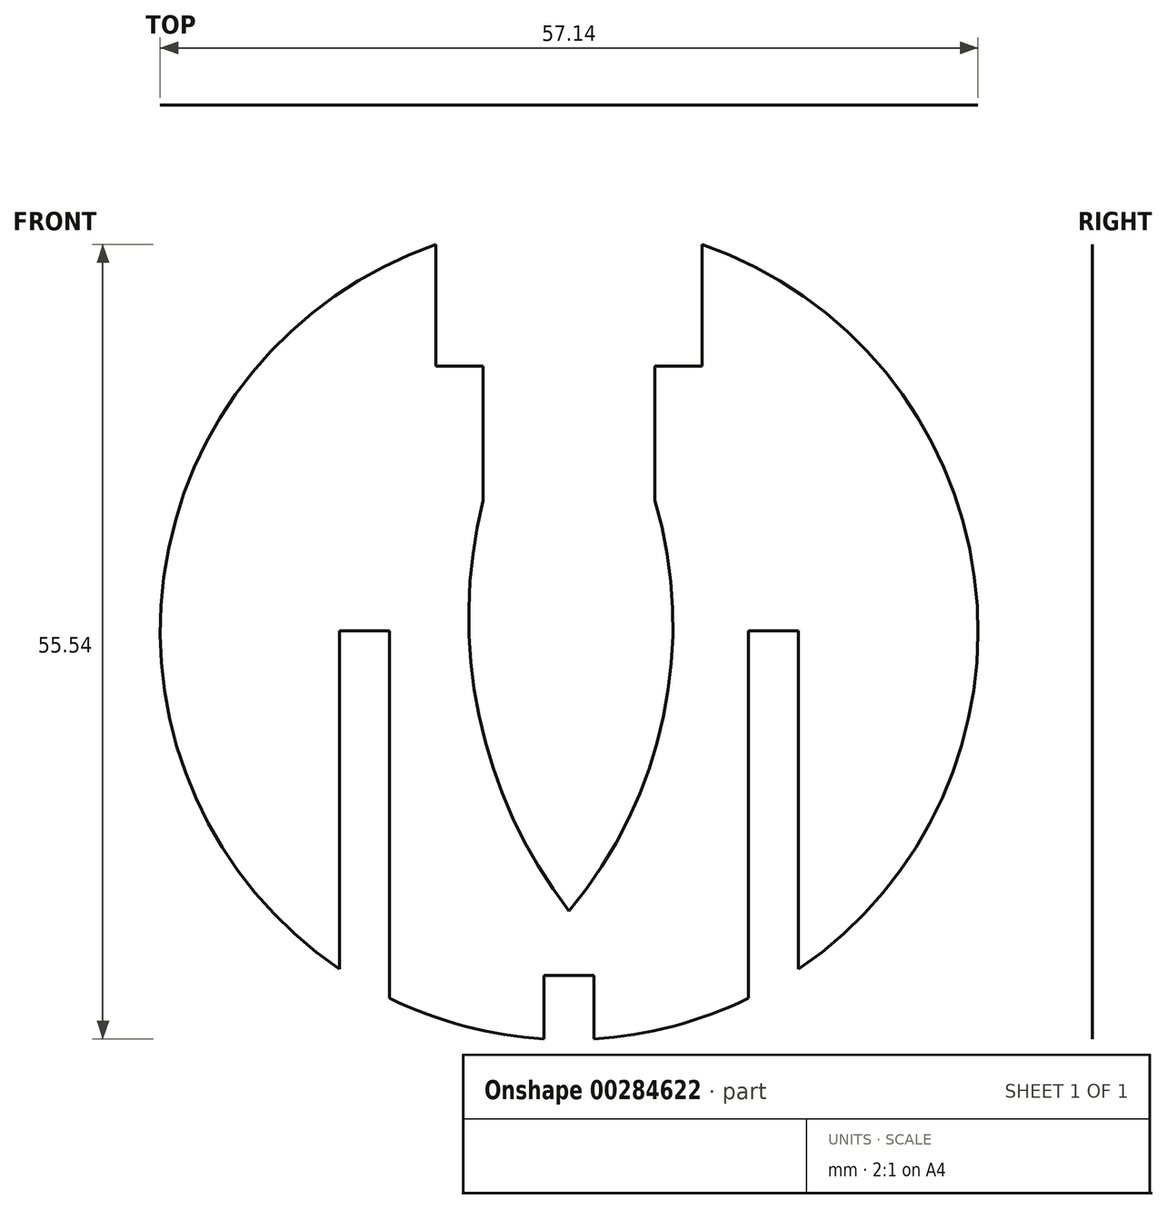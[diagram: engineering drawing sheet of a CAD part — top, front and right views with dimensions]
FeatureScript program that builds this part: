
annotation { "Feature Type Name" : "Feature", "Feature Type Description" : "" }
export const myFeature = defineFeature(function(context is Context, id is Id, definition is map)
    precondition{}
    {
        {
            var Q0;
            Q0=qCreatedBy(makeId("Front.planeOp"),FACE);
            var sketch = newSketch(context, id + "F0", { "sketchPlane" : qUnion([Q0])});
            skCircle(sketch, "E0", {"center": v(0, 0) * mm, "radius": 28.58 * mm});
            skSolve(sketch);
        }
        {
            var Q0;
            Q0 = qSketchRegion(id + "F0", true);
            extrude(context, id + "F1", {"entities" : qUnion([Q0]), "depth" : 1 / 203.2 * mm});
        }
        {
            var Q0;
            Q0=makeQuery(id+"F1.opExtrude","CAP_FACE",FACE,{"disambiguationData":[OSD([sQuery(id+"F0.wireOp",EDGE,"E0")])],"isStart":false});
            var sketch = newSketch(context, id + "F2", { "sketchPlane" : qUnion([Q0])});
            skLineSegment(sketch, "E1", {"start": v(-1.75, -28.52) * mm, "end": v(-1.75, -24.08) * mm});
            skLineSegment(sketch, "E2", {"start": v(-1.75, -24.08) * mm, "end": v(1.75, -24.08) * mm});
            skLineSegment(sketch, "E3", {"start": v(1.75, -24.08) * mm, "end": v(1.75, -28.52) * mm});
            skLineSegment(sketch, "E4", {"start": v(-16.04, -23.65) * mm, "end": v(-16.04, 0) * mm});
            skLineSegment(sketch, "E5", {"start": v(-16.04, 0) * mm, "end": v(-12.54, 0) * mm});
            skLineSegment(sketch, "E6", {"start": v(-12.54, 0) * mm, "end": v(-12.54, -25.68) * mm});
            skLineSegment(sketch, "E7", {"start": v(12.54, -25.68) * mm, "end": v(12.54, 0) * mm});
            skLineSegment(sketch, "E8", {"start": v(12.54, 0) * mm, "end": v(16.04, 0) * mm});
            skLineSegment(sketch, "E9", {"start": v(16.04, 0) * mm, "end": v(16.04, -23.65) * mm});
            skLineSegment(sketch, "E10", {"start": v(0, 0) * mm, "end": v(0, -28.58) * mm});
            skPoint(sketch, "E11", {"position": v(0, -24.08) * mm});
            skLineSegment(sketch, "E12", {"start": v(0, 0) * mm, "end": v(-28.58, 0) * mm});
            skPoint(sketch, "E13", {"position": v(-14.29, 0) * mm});
            skLineSegment(sketch, "E14", {"start": v(0, 0) * mm, "end": v(28.58, 0) * mm});
            skPoint(sketch, "E15", {"position": v(14.29, 0) * mm});
            skLineSegment(sketch, "E16", {"start": v(-9.3, 27.02) * mm, "end": v(-9.3, 18.52) * mm});
            skLineSegment(sketch, "E17", {"start": v(-9.3, 18.52) * mm, "end": v(-6, 18.52) * mm});
            skLineSegment(sketch, "E18", {"start": v(-6, 18.52) * mm, "end": v(-6, 9.13) * mm});
            skLineSegment(sketch, "E19", {"start": v(6, 9.13) * mm, "end": v(6, 18.52) * mm});
            skLineSegment(sketch, "E20", {"start": v(6, 18.52) * mm, "end": v(9.3, 18.52) * mm});
            skLineSegment(sketch, "E21", {"start": v(9.3, 18.52) * mm, "end": v(9.3, 27.02) * mm});
            skArc(sketch, "E22", {"start": v(-6, 9.13) * mm, "mid": v(-6.3, -5.91) * mm, "end": v(0, -19.58) * mm});
            skArc(sketch, "E23", {"start": v(0, -19.58) * mm, "mid": v(6.6, -5.97) * mm, "end": v(6, 9.13) * mm});
            skSolve(sketch);
        }
        {
            var Q0;
            Q0 = qSketchRegion(id + "F2", true);
            var Q1;
            {var subQ10=sQuery(id+"F2.wireOp",EDGE,"E16");Q1=makeQuery(id+"F2.imprint","IMPRINT",FACE,{"disambiguationData":[TD([[makeQuery(id+"F2.imprint","IMPRINT",EDGE,{"derivedFrom":subQ10}),1.0]])]});}
            var Q2;
            {var subQ0=sQuery(id+"F2.wireOp",EDGE,"E4");Q2=makeQuery(id+"F2.imprint","IMPRINT",FACE,{"disambiguationData":[TD([[makeQuery(id+"F2.imprint","IMPRINT",EDGE,{"derivedFrom":subQ0}),-1.0]])]});}
            var Q3;
            {var subQ0=sQuery(id+"F2.wireOp",EDGE,"E1");Q3=makeQuery(id+"F2.imprint","IMPRINT",FACE,{"disambiguationData":[TD([[makeQuery(id+"F2.imprint","IMPRINT",EDGE,{"derivedFrom":subQ0}),-1.0]])]});}
            var Q4;
            {var subQ0=sQuery(id+"F2.wireOp",EDGE,"E3");Q4=makeQuery(id+"F2.imprint","IMPRINT",FACE,{"disambiguationData":[TD([[makeQuery(id+"F2.imprint","IMPRINT",EDGE,{"derivedFrom":subQ0}),-1.0]])]});}
            var Q5;
            {var subQ0=sQuery(id+"F2.wireOp",EDGE,"E7");Q5=makeQuery(id+"F2.imprint","IMPRINT",FACE,{"disambiguationData":[TD([[makeQuery(id+"F2.imprint","IMPRINT",EDGE,{"derivedFrom":subQ0}),-1.0]])]});}
            extrude(context, id + "F3", {"entities" : qUnion([Q0, Q1, Q2, Q3, Q4, Q5]), "operationType" : NewBodyOperationType.REMOVE, "endBound" : BoundingType.THROUGH_ALL, "oppositeDirection" : true, "depth" : 25 * mm});
        }
    });
